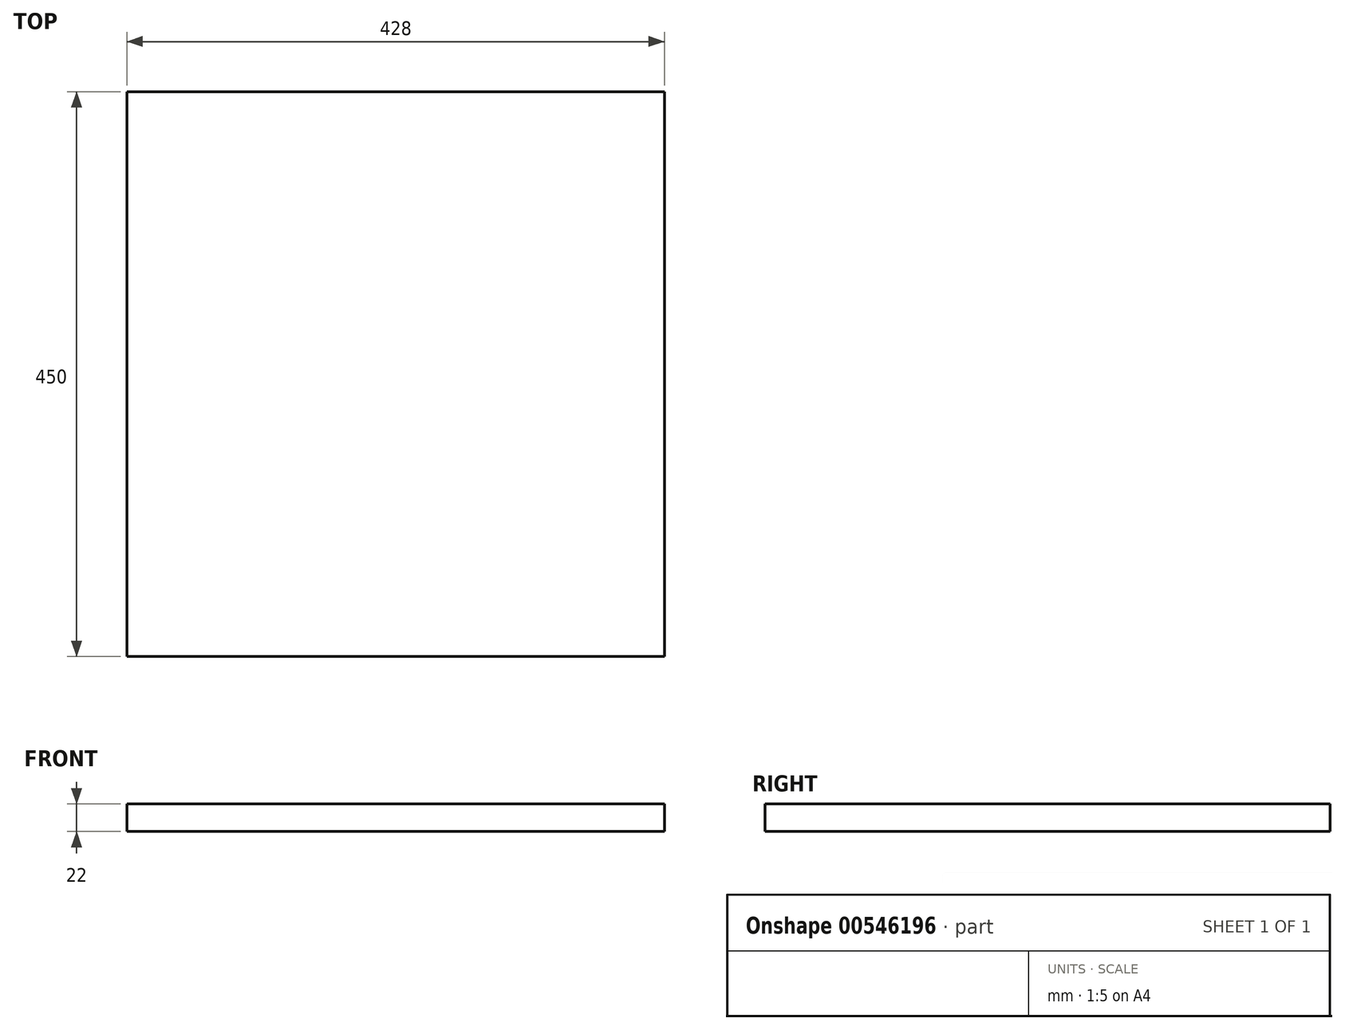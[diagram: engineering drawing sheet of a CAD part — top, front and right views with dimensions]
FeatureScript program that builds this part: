
annotation { "Feature Type Name" : "Feature", "Feature Type Description" : "" }
export const myFeature = defineFeature(function(context is Context, id is Id, definition is map)
    precondition{}
    {
        {
            var Q0;
            Q0=qCreatedBy(makeId("Top.planeOp"),FACE);
            var sketch = newSketch(context, id + "F0", { "sketchPlane" : qUnion([Q0])});
            skLineSegment(sketch, "E0.bottom", {"start": v(0, 0) * mm, "end": v(-428, 0) * mm});
            skLineSegment(sketch, "E0.top", {"start": v(0, 450) * mm, "end": v(-428, 450) * mm});
            skLineSegment(sketch, "E0.left", {"start": v(0, 0) * mm, "end": v(0, 450) * mm});
            skLineSegment(sketch, "E0.right", {"start": v(-428, 0) * mm, "end": v(-428, 450) * mm});
            skSolve(sketch);
        }
        {
            var Q0;
            Q0 = qSketchRegion(id + "F0", true);
            extrude(context, id + "F1", {"entities" : qUnion([Q0]), "oppositeDirection" : true, "depth" : 22 * mm, "offsetDistance" : 25 * mm});
        }
    });
